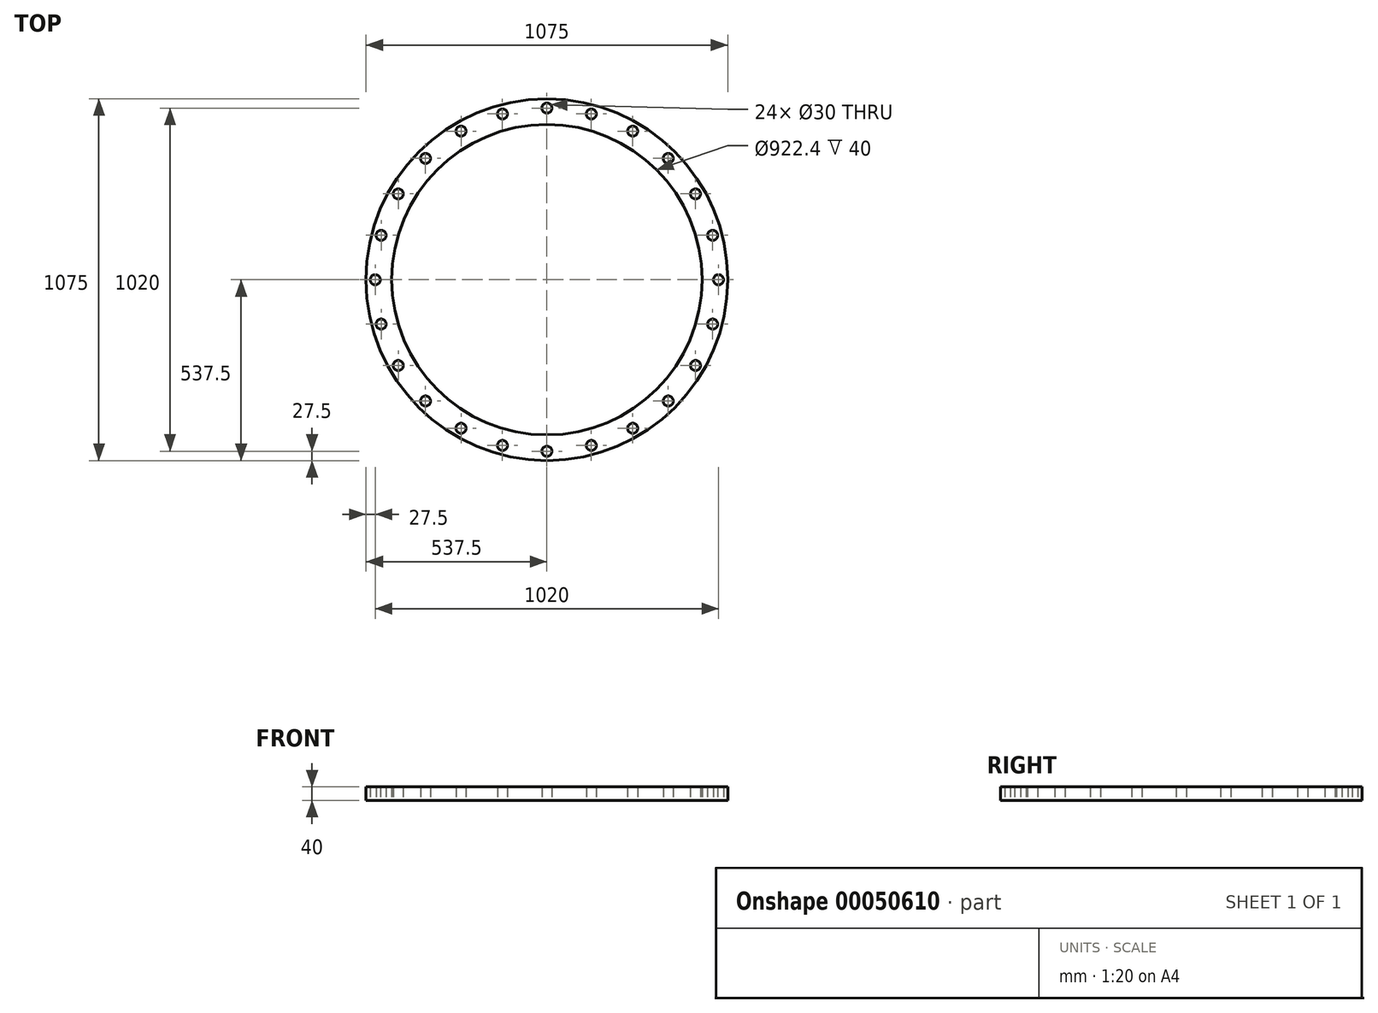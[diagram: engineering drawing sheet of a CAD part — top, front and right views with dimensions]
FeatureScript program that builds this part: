
annotation { "Feature Type Name" : "Feature", "Feature Type Description" : "" }
export const myFeature = defineFeature(function(context is Context, id is Id, definition is map)
    precondition{}
    {
        {
            assignVariable(context, id + "F0", {"name" : "C4", "anyValue" : 40});
        }
        {
            assignVariable(context, id + "F1", {"name" : "C6", "anyValue" : 24});
        }
        {
            var Q0;
            Q0=qCreatedBy(makeId("Top.planeOp"),FACE);
            var sketch = newSketch(context, id + "F2", { "sketchPlane" : qUnion([Q0])});
            skCircle(sketch, "E0", {"center": v(0, 0) * mm, "radius": 537.5 * mm});
            skCircle(sketch, "E1", {"center": v(0, 0) * mm, "radius": 461.2 * mm});
            skCircle(sketch, "E2", {"center": v(0, 0) * mm, "radius": 510 * mm, "construction": true});
            skCircle(sketch, "E3", {"center": v(0, 510) * mm, "radius": 15 * mm});
            skSolve(sketch);
        }
        {
            var Q0;
            Q0=makeQuery(id+"F2.imprint","IMPRINT",FACE,{"disambiguationData":[TD([[makeQuery(id+"F2.imprint","IMPRINT",EDGE,{"derivedFrom":sQuery(id+"F2.wireOp",EDGE,"E0")}),1.0]])]});
            extrude(context, id + "F3", {"entities" : qUnion([Q0]), "depth" : (getVariable(context, 'C4')) * mm});
        }
        {
            var Q0;
            Q0=makeQuery(id+"F3.opExtrude","SWEPT_FACE",FACE,{"disambiguationData":[OSD([sQuery(id+"F2.wireOp",EDGE,"E3")])]});
            var Q1;
            Q1=makeQuery(id+"F3.opExtrude","CAP_EDGE",EDGE,{"disambiguationData":[OSD([sQuery(id+"F2.wireOp",EDGE,"E1")])],"isStart":false});
            circularPattern(context, id + "F4", {"patternType" : PatternType.FACE, "faces" : qUnion([Q0]), "axis" : qUnion([Q1]), "angle" : 360 * degree, "instanceCount" : getVariable(context, 'C6'), "equalSpace" : true});
        }
    });
